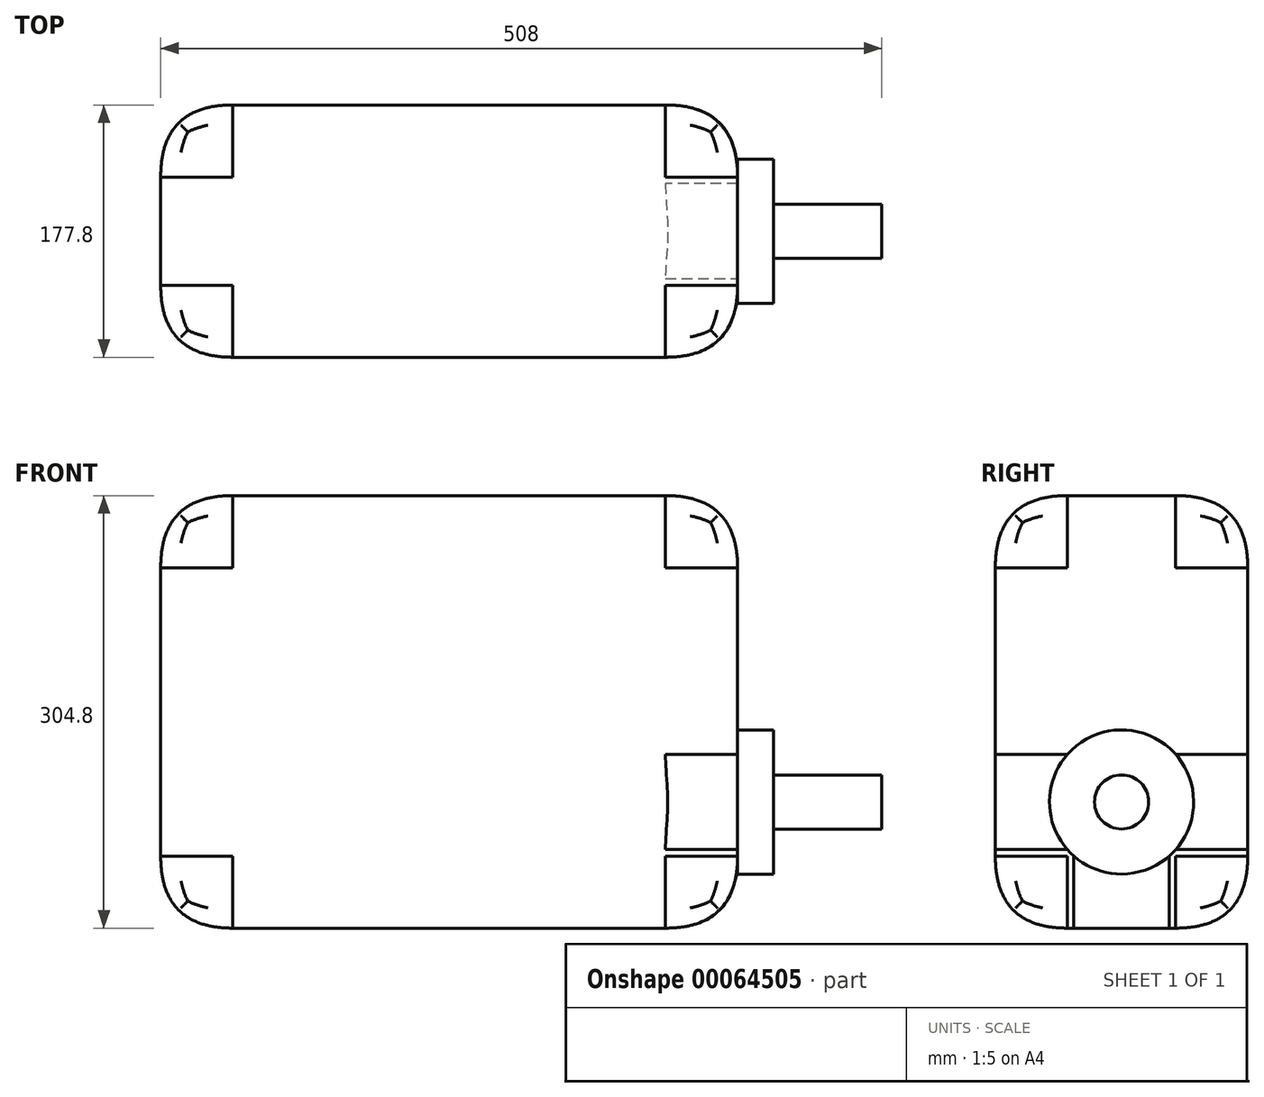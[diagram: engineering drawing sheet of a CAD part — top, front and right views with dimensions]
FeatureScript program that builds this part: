
annotation { "Feature Type Name" : "Feature", "Feature Type Description" : "" }
export const myFeature = defineFeature(function(context is Context, id is Id, definition is map)
    precondition{}
    {
        {
            var Q0;
            Q0=qCreatedBy(makeId("Top.planeOp"),FACE);
            var sketch = newSketch(context, id + "F0", { "sketchPlane" : qUnion([Q0])});
            skLineSegment(sketch, "E0.rect.bottom", {"start": v(203.2, 88.9) * mm, "end": v(-203.2, 88.9) * mm});
            skLineSegment(sketch, "E0.rect.top", {"start": v(203.2, -88.9) * mm, "end": v(-203.2, -88.9) * mm});
            skLineSegment(sketch, "E0.rect.left", {"start": v(203.2, 88.9) * mm, "end": v(203.2, -88.9) * mm});
            skLineSegment(sketch, "E0.rect.right", {"start": v(-203.2, 88.9) * mm, "end": v(-203.2, -88.9) * mm});
            skPoint(sketch, "E0.rect.middle", {"position": v(0, 0) * mm});
            skSolve(sketch);
        }
        {
            var Q0;
            Q0 = qSketchRegion(id + "F0", true);
            extrude(context, id + "F1", {"entities" : qUnion([Q0]), "depth" : 304.8 * mm});
        }
        {
            var Q0;
            Q0=makeQuery(id+"F1.opExtrude","SWEPT_FACE",FACE,{"disambiguationData":[OSD([sQuery(id+"F0.wireOp",EDGE,"E0.rect.left")])]});
            var sketch = newSketch(context, id + "F2", { "sketchPlane" : qUnion([Q0])});
            skLineSegment(sketch, "E1", {"start": v(0, 0) * mm, "end": v(0, 304.8) * mm, "construction": true});
            skCircle(sketch, "E2", {"center": v(0, 88.9) * mm, "radius": 50.8 * mm});
            skSolve(sketch);
        }
        {
            var Q0;
            Q0=makeQuery(id+"F2.imprint","IMPRINT",FACE,{"disambiguationData":[TD([[makeQuery(id+"F2.imprint","IMPRINT",EDGE,{"derivedFrom":sQuery(id+"F2.wireOp",EDGE,"E2")}),1.0]])]});
            extrude(context, id + "F3", {"entities" : qUnion([Q0]), "operationType" : NewBodyOperationType.ADD, "depth" : 25.4 * mm});
        }
        {
            var Q0;
            Q0=makeQuery(id+"F3.opExtrude","CAP_FACE",FACE,{"disambiguationData":[OSD([sQuery(id+"F2.wireOp",EDGE,"E2")])],"isStart":false});
            var sketch = newSketch(context, id + "F4", { "sketchPlane" : qUnion([Q0])});
            skCircle(sketch, "E3", {"center": v(0, 88.9) * mm, "radius": 19.05 * mm});
            skSolve(sketch);
        }
        {
            var Q0;
            Q0=makeQuery(id+"F4.imprint","IMPRINT",FACE,{"disambiguationData":[TD([[makeQuery(id+"F4.imprint","IMPRINT",EDGE,{"derivedFrom":sQuery(id+"F4.wireOp",EDGE,"E3")}),1.0]])]});
            extrude(context, id + "F5", {"entities" : qUnion([Q0]), "operationType" : NewBodyOperationType.ADD, "depth" : 76.2 * mm});
        }
        {
            var Q0;
            Q0=makeQuery(id+"F5.opExtrude","CAP_FACE",FACE,{"disambiguationData":[OSD([sQuery(id+"F4.wireOp",EDGE,"E3")])],"isStart":false});
            var sketch = newSketch(context, id + "F6", { "sketchPlane" : qUnion([Q0])});
            skCircle(sketch, "E4", {"center": v(0, 88.9) * mm, "radius": 15.88 * mm});
            skSolve(sketch);
        }
        {
            var Q0;
            Q0=sQuery(id+"F6.wireOp",EDGE,"E4");
            extrude(context, id + "F7", {"bodyType" : ToolBodyType.SURFACE, "surfaceEntities" : qUnion([Q0]), "oppositeDirection" : true, "depth" : 76.2 * mm});
        }
        {
            var Q0;
            Q0=makeQuery(id+"F1.opExtrude","CAP_FACE",FACE,{"disambiguationData":[OSD([sQuery(id+"F0.wireOp",EDGE,"E0.rect.bottom"),sQuery(id+"F0.wireOp",EDGE,"E0.rect.top"),sQuery(id+"F0.wireOp",EDGE,"E0.rect.left"),sQuery(id+"F0.wireOp",EDGE,"E0.rect.right")])],"isStart":true});
            cPlane(context, id + "F8", {"entities" : qUnion([Q0]), "cplaneType" : CPlaneType.OFFSET, "offset" : 38.1 * mm, "oppositeDirection" : true, "width" : 152.4 * mm, "height" : 152.4 * mm});
        }
        {
            var Q0;
            Q0=qCreatedBy(id+"F8.planeOp",FACE);
            var sketch = newSketch(context, id + "F9", { "sketchPlane" : qUnion([Q0])});
            skCircle(sketch, "E5", {"center": v(327.66, 0) * mm, "radius": 19.05 * mm});
            skSolve(sketch);
        }
        {
            var Q0;
            Q0=makeQuery(id+"F9.imprint","IMPRINT",FACE,{"disambiguationData":[TD([[makeQuery(id+"F9.imprint","IMPRINT",EDGE,{"derivedFrom":sQuery(id+"F9.wireOp",EDGE,"E5")}),1.0]])]});
            extrude(context, id + "F10", {"entities" : qUnion([Q0]), "oppositeDirection" : true, "depth" : 76.2 * mm});
        }
        {
            var Q0;
            Q0=makeQuery(id+"F10.opExtrude","CAP_FACE",FACE,{"disambiguationData":[OSD([sQuery(id+"F9.wireOp",EDGE,"E5")])],"isStart":true});
            shell(context, id + "F11", {"entities" : qUnion([Q0]), "thickness" : 6.35 * mm});
        }
        {
            var Q0;
            Q0=makeQuery(id+"F10.opExtrude","SWEPT_BODY",BODY,{"disambiguationData":[OSD([sQuery(id+"F9.wireOp",EDGE,"E5")])]});
            deleteBodies(context, id + "F12", {"entities" : qUnion([Q0])});
        }
        {
            var Q0;
            Q0=makeQuery(id+"F1.opExtrude","SWEPT_FACE",FACE,{"disambiguationData":[OSD([sQuery(id+"F0.wireOp",EDGE,"E0.rect.top")])]});
            var Q1;
            Q1=makeQuery(id+"F1.opExtrude","CAP_FACE",FACE,{"disambiguationData":[OSD([sQuery(id+"F0.wireOp",EDGE,"E0.rect.bottom"),sQuery(id+"F0.wireOp",EDGE,"E0.rect.top"),sQuery(id+"F0.wireOp",EDGE,"E0.rect.left"),sQuery(id+"F0.wireOp",EDGE,"E0.rect.right")])],"isStart":false});
            var Q2;
            Q2=makeQuery(id+"F1.opExtrude","SWEPT_FACE",FACE,{"disambiguationData":[OSD([sQuery(id+"F0.wireOp",EDGE,"E0.rect.bottom")])]});
            var Q3;
            Q3=makeQuery(id+"F1.opExtrude","CAP_FACE",FACE,{"disambiguationData":[OSD([sQuery(id+"F0.wireOp",EDGE,"E0.rect.bottom"),sQuery(id+"F0.wireOp",EDGE,"E0.rect.top"),sQuery(id+"F0.wireOp",EDGE,"E0.rect.left"),sQuery(id+"F0.wireOp",EDGE,"E0.rect.right")])],"isStart":true});
            fillet(context, id + "F13", {"entities" : qUnion([Q0, Q1, Q2, Q3]), "radius" : 50.8 * mm, "tangentPropagation" : true, "rho" : 0.5, "crossSection" : FilletCrossSection.CONIC, "allowEdgeOverflow" : false});
        }
    });
